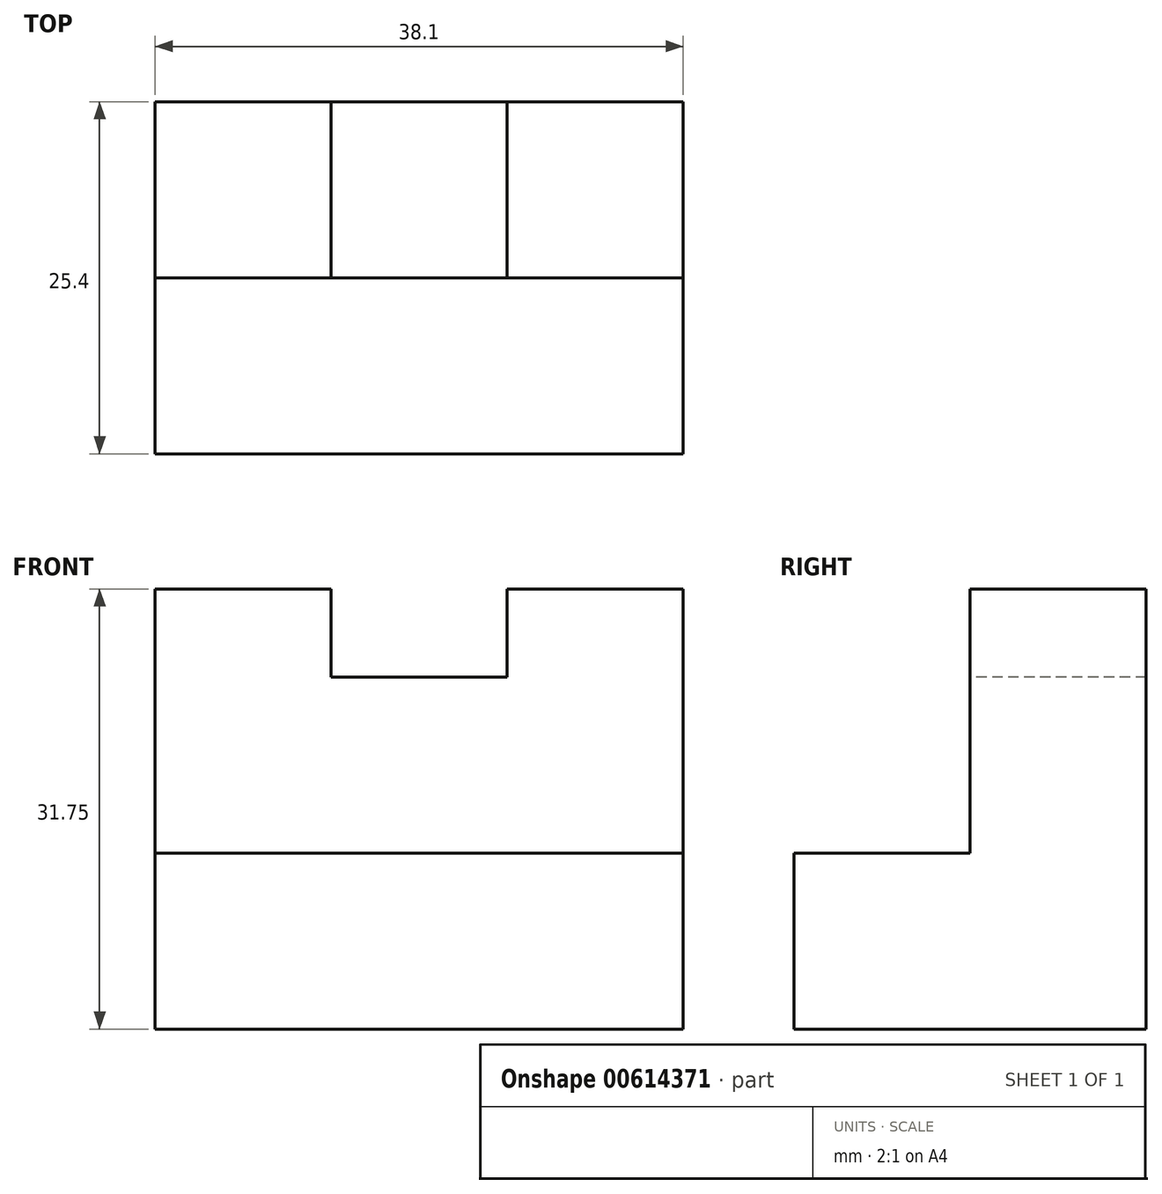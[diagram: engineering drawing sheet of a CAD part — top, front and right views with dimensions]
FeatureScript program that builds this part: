
annotation { "Feature Type Name" : "Feature", "Feature Type Description" : "" }
export const myFeature = defineFeature(function(context is Context, id is Id, definition is map)
    precondition{}
    {
        {
            var Q0;
            Q0=qCreatedBy(makeId("Top.planeOp"),FACE);
            var sketch = newSketch(context, id + "F0", { "sketchPlane" : qUnion([Q0])});
            skLineSegment(sketch, "E0", {"start": v(0, 0) * mm, "end": v(38.1, 0) * mm});
            skLineSegment(sketch, "E1", {"start": v(38.1, 0) * mm, "end": v(38.1, 25.4) * mm});
            skLineSegment(sketch, "E2", {"start": v(38.1, 25.4) * mm, "end": v(0, 25.4) * mm});
            skLineSegment(sketch, "E3", {"start": v(0, 25.4) * mm, "end": v(0, 0) * mm});
            skSolve(sketch);
        }
        {
            var Q0;
            Q0=makeQuery(id+"F0.imprint","IMPRINT",FACE,{"disambiguationData":[TD([[makeQuery(id+"F0.imprint","IMPRINT",EDGE,{"derivedFrom":sQuery(id+"F0.wireOp",EDGE,"E0")}),1.0]])]});
            extrude(context, id + "F1", {"entities" : qUnion([Q0]), "depth" : 31.75 * mm, "offsetDistance" : 25.4 * mm});
        }
        {
            var Q0;
            Q0=makeQuery(id+"F1.opExtrude","CAP_FACE",FACE,{"disambiguationData":[OSD([sQuery(id+"F0.wireOp",EDGE,"E0"),sQuery(id+"F0.wireOp",EDGE,"E1"),sQuery(id+"F0.wireOp",EDGE,"E2"),sQuery(id+"F0.wireOp",EDGE,"E3")])],"isStart":false});
            var sketch = newSketch(context, id + "F2", { "sketchPlane" : qUnion([Q0])});
            skLineSegment(sketch, "E4", {"start": v(0, 0) * mm, "end": v(0, 12.7) * mm});
            skLineSegment(sketch, "E5", {"start": v(0, 12.7) * mm, "end": v(38.1, 12.7) * mm});
            skSolve(sketch);
        }
        {
            var Q0;
            Q0=makeQuery(id+"F2.imprint","IMPRINT",FACE,{"disambiguationData":[TD([[makeQuery(id+"F2.imprint","IMPRINT",EDGE,{"derivedFrom":sQuery(id+"F2.wireOp",EDGE,"E4")}),1.0]])]});
            extrude(context, id + "F3", {"entities" : qUnion([Q0]), "operationType" : NewBodyOperationType.REMOVE, "oppositeDirection" : true, "depth" : 19.05 * mm, "offsetDistance" : 25.4 * mm});
        }
        {
            var Q0;
            Q0=makeQuery(id+"F1.opExtrude","CAP_FACE",FACE,{"disambiguationData":[OSD([sQuery(id+"F0.wireOp",EDGE,"E0"),sQuery(id+"F0.wireOp",EDGE,"E1"),sQuery(id+"F0.wireOp",EDGE,"E2"),sQuery(id+"F0.wireOp",EDGE,"E3")])],"isStart":false});
            var sketch = newSketch(context, id + "F4", { "sketchPlane" : qUnion([Q0])});
            skLineSegment(sketch, "E6", {"start": v(0, 25.4) * mm, "end": v(12.7, 25.4) * mm});
            skLineSegment(sketch, "E7", {"start": v(38.1, 25.4) * mm, "end": v(25.4, 25.4) * mm});
            skLineSegment(sketch, "E8", {"start": v(25.4, 25.4) * mm, "end": v(25.4, 12.7) * mm});
            skLineSegment(sketch, "E9", {"start": v(12.7, 25.4) * mm, "end": v(12.7, 12.7) * mm});
            skSolve(sketch);
        }
        {
            var Q0;
            Q0 = qSketchRegion(id + "F4", true);
            var Q1;
            {var subQ0=sQuery(id+"F4.wireOp",EDGE,"E8");Q1=makeQuery(id+"F4.imprint","IMPRINT",FACE,{"disambiguationData":[TD([[makeQuery(id+"F4.imprint","IMPRINT",EDGE,{"derivedFrom":subQ0}),-1.0]])]});}
            extrude(context, id + "F5", {"entities" : qUnion([Q0, Q1]), "operationType" : NewBodyOperationType.REMOVE, "oppositeDirection" : true, "depth" : 6.35 * mm, "offsetDistance" : 25.4 * mm});
        }
    });
